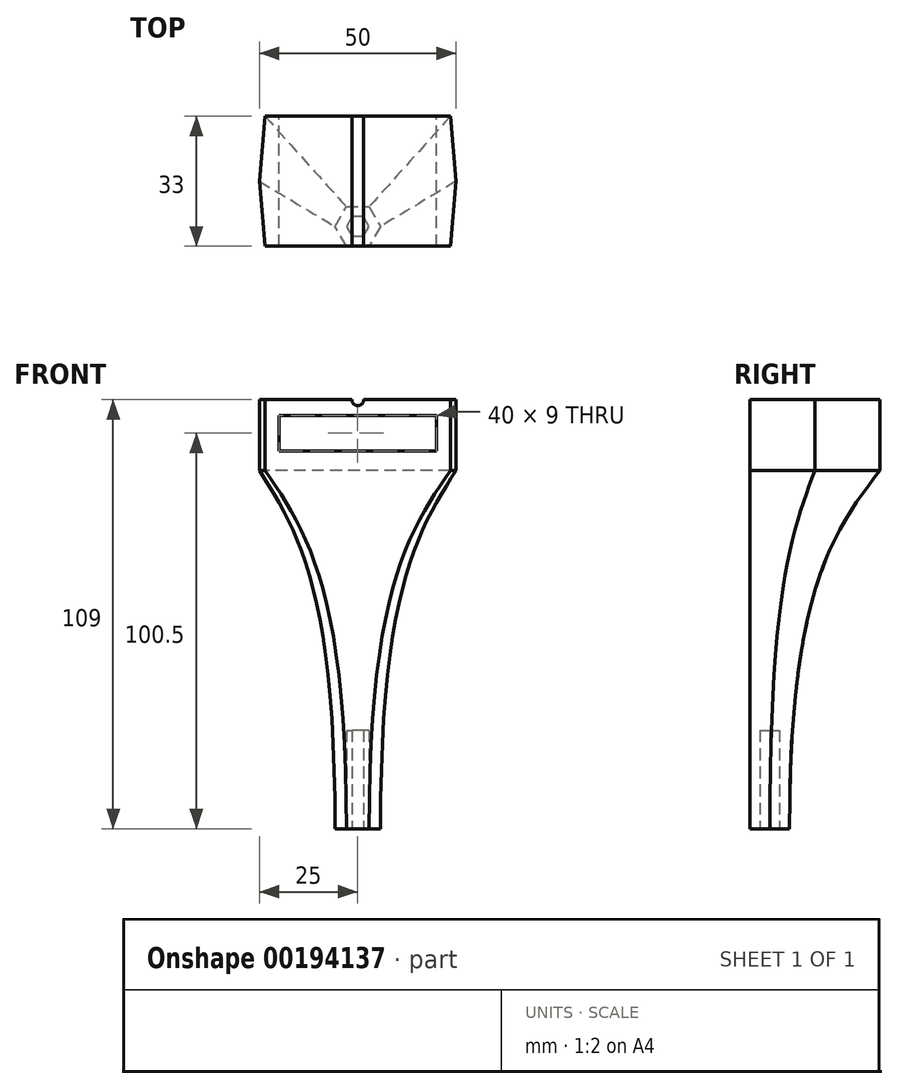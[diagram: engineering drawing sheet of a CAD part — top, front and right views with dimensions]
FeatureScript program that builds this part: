
annotation { "Feature Type Name" : "Feature", "Feature Type Description" : "" }
export const myFeature = defineFeature(function(context is Context, id is Id, definition is map)
    precondition{}
    {
        {
            var Q0;
            Q0=qCreatedBy(makeId("Top.planeOp"),FACE);
            var sketch = newSketch(context, id + "F0", { "sketchPlane" : qUnion([Q0])});
            skCircle(sketch, "E0", {"center": v(0, 0) * mm, "radius": 2.38 * mm});
            skCircle(sketch, "E1", {"center": v(0, 0) * mm, "radius": 4.5 * mm});
            skCircle(sketch, "E2.cCircle", {"center": v(0, 0) * mm, "radius": 5.2 * mm, "construction": true});
            skLineSegment(sketch, "E2.0", {"start": v(0, 5.2) * mm, "end": v(4.5, 2.6) * mm});
            skLineSegment(sketch, "E2.1", {"start": v(4.5, 2.6) * mm, "end": v(4.5, -2.6) * mm});
            skLineSegment(sketch, "E2.2", {"start": v(4.5, -2.6) * mm, "end": v(0, -5.2) * mm});
            skLineSegment(sketch, "E2.3", {"start": v(0, -5.2) * mm, "end": v(-4.5, -2.6) * mm});
            skLineSegment(sketch, "E2.4", {"start": v(-4.5, -2.6) * mm, "end": v(-4.5, 2.6) * mm});
            skLineSegment(sketch, "E2.5", {"start": v(-4.5, 2.6) * mm, "end": v(0, 5.2) * mm});
            skSolve(sketch);
        }
        {
            var Q0;
            Q0=makeQuery(id+"F0.imprint","IMPRINT",FACE,{"disambiguationData":[TD([[makeQuery(id+"F0.imprint","IMPRINT",EDGE,{"derivedFrom":sQuery(id+"F0.wireOp",EDGE,"E0")}),1.0]])]});
            extrude(context, id + "F1", {"entities" : qUnion([Q0]), "depth" : 24 * mm});
        }
        {
            var Q0;
            Q0=makeQuery(id+"F1.opExtrude","CAP_FACE",FACE,{"disambiguationData":[OSD([sQuery(id+"F0.wireOp",EDGE,"E0")])],"isStart":false});
            var sketch = newSketch(context, id + "F2", { "sketchPlane" : qUnion([Q0])});
            skCircle(sketch, "E3.cCircle", {"center": v(0, 0) * mm, "radius": 5.77 * mm, "construction": true});
            skLineSegment(sketch, "E3.0", {"start": v(5.77, 0) * mm, "end": v(2.89, -5) * mm});
            skLineSegment(sketch, "E3.1", {"start": v(2.89, -5) * mm, "end": v(-2.89, -5) * mm});
            skLineSegment(sketch, "E3.2", {"start": v(-2.89, -5) * mm, "end": v(-5.77, 0) * mm});
            skLineSegment(sketch, "E3.3", {"start": v(-5.77, 0) * mm, "end": v(-2.89, 5) * mm});
            skLineSegment(sketch, "E3.4", {"start": v(-2.89, 5) * mm, "end": v(2.89, 5) * mm});
            skLineSegment(sketch, "E3.5", {"start": v(2.89, 5) * mm, "end": v(5.77, 0) * mm});
            skSolve(sketch);
        }
        {
            var Q0;
            Q0=qCreatedBy(makeId("Top.planeOp"),FACE);
            cPlane(context, id + "F3", {"entities" : qUnion([Q0]), "cplaneType" : CPlaneType.OFFSET, "offset" : 115 * mm, "width" : 150 * mm, "height" : 150 * mm});
        }
        {
            var Q0;
            Q0=qCreatedBy(id+"F3.planeOp",FACE);
            var sketch = newSketch(context, id + "F4", { "sketchPlane" : qUnion([Q0])});
            skLineSegment(sketch, "E4.bottom", {"start": v(23.56, -5) * mm, "end": v(-23.56, -5) * mm});
            skLineSegment(sketch, "E4.top", {"start": v(23.56, 28) * mm, "end": v(-23.56, 28) * mm});
            skPoint(sketch, "E4.middle", {"position": v(0, 12) * mm});
            skLineSegment(sketch, "E5", {"start": v(-25, 11.5) * mm, "end": v(-23.56, -5) * mm});
            skLineSegment(sketch, "E6", {"start": v(-25, 11.5) * mm, "end": v(-23.56, 28) * mm});
            skLineSegment(sketch, "E7", {"start": v(23.56, 28) * mm, "end": v(25, 11.5) * mm});
            skLineSegment(sketch, "E8", {"start": v(25, 11.5) * mm, "end": v(23.56, -5) * mm});
            skLineSegment(sketch, "E9", {"start": v(0, 0) * mm, "end": v(0, -5) * mm});
            skPoint(sketch, "E9.endSnap0", {"position": v(0, -5) * mm});
            skSolve(sketch);
        }
        {
            var Q1;
            Q1=makeQuery(id+"F4.imprint","IMPRINT",FACE,{"disambiguationData":[TD([[makeQuery(id+"F4.imprint","IMPRINT",EDGE,{"derivedFrom":sQuery(id+"F4.wireOp",EDGE,"E4.bottom")}),-1.0]])]});
            var Q2;
            Q2 = qSketchRegion(id + "F2", true);
            var Q3;
            Q3=sQuery(id+"F2.wireOp",VERTEX,"E3.1.start");
            var Q4;
            Q4=sQuery(id+"F4.wireOp",VERTEX,"E8.end");
            loft(context, id + "F5", {"operationType" : NewBodyOperationType.ADD, "endCondition" : LoftEndDerivativeType.NORMAL_TO_PROFILE, "endMagnitude" : 2, "sheetProfilesArray" : [{ "sheetProfileEntities" : qUnion([Q1]) }, { "sheetProfileEntities" : qUnion([Q2]) }], "matchConnections" : true, "connections" : [{ "connectionEntities" : qUnion([Q3, Q4]), "connectionEdgeQueries" : qUnion([]), "connectionEdgeParameters" : [] }]});
        }
        {
            var Q0;
            Q0=makeQuery(id+"F5.opLoft","CAP_FACE",FACE,{"disambiguationData":[OSD([makeQuery(id+"F4.imprint","IMPRINT",FACE,{"disambiguationData":[TD([[makeQuery(id+"F4.imprint","IMPRINT",EDGE,{"derivedFrom":sQuery(id+"F4.wireOp",EDGE,"E4.bottom")}),-1.0]])]})])],"isStart":true});
            extrude(context, id + "F6", {"entities" : qUnion([Q0]), "operationType" : NewBodyOperationType.ADD, "depth" : 18 * mm});
        }
        {
            var Q0;
            Q0=makeQuery(id+"F6.opExtrude","SWEPT_FACE",FACE,{"disambiguationData":[OSD([sQuery(id+"F4.wireOp",EDGE,"E4.top"),sQuery(id+"F4.wireOp",EDGE,"E4.left"),sQuery(id+"F4.wireOp",EDGE,"E4.right")])]});
            var sketch = newSketch(context, id + "F7", { "sketchPlane" : qUnion([Q0])});
            skLineSegment(sketch, "E10.bottom", {"start": v(-20, 120) * mm, "end": v(20, 120) * mm});
            skLineSegment(sketch, "E10.top", {"start": v(-20, 129) * mm, "end": v(20, 129) * mm});
            skLineSegment(sketch, "E10.left", {"start": v(-20, 120) * mm, "end": v(-20, 129) * mm});
            skLineSegment(sketch, "E10.right", {"start": v(20, 120) * mm, "end": v(20, 129) * mm});
            skPoint(sketch, "E10.middle", {"position": v(0, 124.5) * mm});
            skCircle(sketch, "E11", {"center": v(0, 133) * mm, "radius": 1.5 * mm});
            skSolve(sketch);
        }
        {
            var Q0;
            Q0 = qSketchRegion(id + "F7", true);
            extrude(context, id + "F8", {"entities" : qUnion([Q0]), "operationType" : NewBodyOperationType.REMOVE, "oppositeDirection" : true, "depth" : 44.4 * mm});
        }
        {
            var Q0;
            Q0=qCreatedBy(makeId("Top.planeOp"),FACE);
            var sketch = newSketch(context, id + "F9", { "sketchPlane" : qUnion([Q0])});
            skLineSegment(sketch, "E12.0", {"start": v(-2.89, 0) * mm, "end": v(-1.44, 2.5) * mm});
            skLineSegment(sketch, "E12.1", {"start": v(-1.44, 2.5) * mm, "end": v(1.44, 2.5) * mm});
            skLineSegment(sketch, "E12.2", {"start": v(1.44, 2.5) * mm, "end": v(2.89, 0) * mm});
            skLineSegment(sketch, "E12.3", {"start": v(2.89, 0) * mm, "end": v(1.44, -2.5) * mm});
            skLineSegment(sketch, "E12.4", {"start": v(1.44, -2.5) * mm, "end": v(-1.44, -2.5) * mm});
            skLineSegment(sketch, "E12.5", {"start": v(-1.44, -2.5) * mm, "end": v(-2.89, 0) * mm});
            skSolve(sketch);
        }
        {
            var Q0;
            Q0 = qSketchRegion(id + "F9", true);
            extrude(context, id + "F10", {"entities" : qUnion([Q0]), "operationType" : NewBodyOperationType.REMOVE, "depth" : (24 + 25) * mm});
        }
    });
